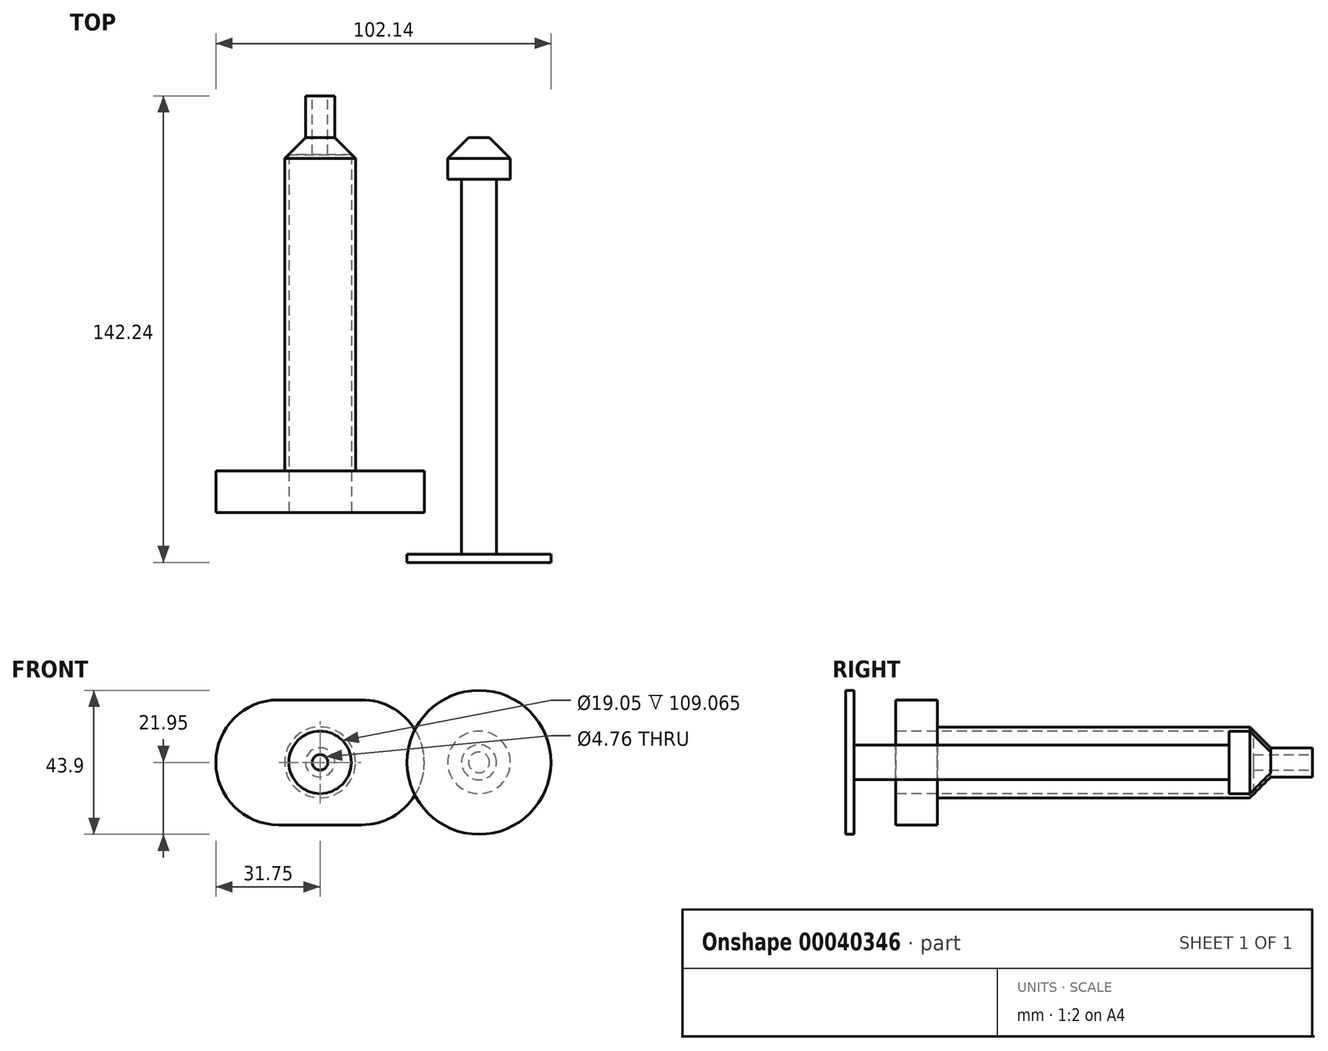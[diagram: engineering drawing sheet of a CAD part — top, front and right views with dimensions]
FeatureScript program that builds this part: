
annotation { "Feature Type Name" : "Feature", "Feature Type Description" : "" }
export const myFeature = defineFeature(function(context is Context, id is Id, definition is map)
    precondition{}
    {
        {
            var Q0;
            Q0=qCreatedBy(makeId("Front.planeOp"),FACE);
            var sketch = newSketch(context, id + "F0", { "sketchPlane" : qUnion([Q0])});
            skCircle(sketch, "E0", {"center": v(0, 0) * mm, "radius": 10.8 * mm});
            skCircle(sketch, "E1", {"center": v(48.44, 0) * mm, "radius": 9.53 * mm});
            skSolve(sketch);
        }
        {
            var Q0;
            Q0=makeQuery(id+"F0.imprint","IMPRINT",FACE,{"disambiguationData":[TD([[makeQuery(id+"F0.imprint","IMPRINT",EDGE,{"derivedFrom":sQuery(id+"F0.wireOp",EDGE,"E0")}),1.0]])]});
            extrude(context, id + "F1", {"entities" : qUnion([Q0]), "depth" : 101.6 * mm});
        }
        {
            var Q0;
            Q0=makeQuery(id+"F1.opExtrude","CAP_EDGE",EDGE,{"disambiguationData":[OSD([sQuery(id+"F0.wireOp",EDGE,"E0")])],"isStart":true});
            chamfer(context, id + "F2", {"entities" : qUnion([Q0]), "width" : 6.35 * mm, "tangentPropagation" : true});
        }
        {
            var Q0;
            Q0=makeQuery(id+"F1.opExtrude","CAP_FACE",FACE,{"disambiguationData":[OSD([sQuery(id+"F0.wireOp",EDGE,"E0")])],"isStart":true});
            extrude(context, id + "F3", {"entities" : qUnion([Q0]), "operationType" : NewBodyOperationType.ADD, "depth" : 12.7 * mm});
        }
        {
            var Q0;
            Q0=makeQuery(id+"F1.opExtrude","CAP_FACE",FACE,{"disambiguationData":[OSD([sQuery(id+"F0.wireOp",EDGE,"E0")])],"isStart":false});
            var sketch = newSketch(context, id + "F4", { "sketchPlane" : qUnion([Q0])});
            skLineSegment(sketch, "E2.rect.bottom", {"start": v(31.75, -19.05) * mm, "end": v(-31.75, -19.05) * mm});
            skLineSegment(sketch, "E2.rect.top", {"start": v(31.75, 19.05) * mm, "end": v(-31.75, 19.05) * mm});
            skLineSegment(sketch, "E2.rect.left", {"start": v(31.75, -19.05) * mm, "end": v(31.75, 19.05) * mm});
            skLineSegment(sketch, "E2.rect.right", {"start": v(-31.75, -19.05) * mm, "end": v(-31.75, 19.05) * mm});
            skPoint(sketch, "E2.rect.middle", {"position": v(0, 0) * mm});
            skSolve(sketch);
        }
        {
            var Q0;
            Q0 = qSketchRegion(id + "F4", true);
            extrude(context, id + "F5", {"entities" : qUnion([Q0]), "operationType" : NewBodyOperationType.ADD, "depth" : 12.7 * mm});
        }
        {
            var Q0;
            Q0=makeQuery(id+"F5.opExtrude","SWEPT_EDGE",EDGE,{"disambiguationData":[OSD([sQuery(id+"F4.wireOp",EDGE,"E2.rect.top"),sQuery(id+"F4.wireOp",EDGE,"E2.rect.right")])]});
            var Q1;
            Q1=makeQuery(id+"F5.opExtrude","SWEPT_EDGE",EDGE,{"disambiguationData":[OSD([sQuery(id+"F4.wireOp",EDGE,"E2.rect.top"),sQuery(id+"F4.wireOp",EDGE,"E2.rect.left")])]});
            var Q2;
            Q2=makeQuery(id+"F5.opExtrude","SWEPT_EDGE",EDGE,{"disambiguationData":[OSD([sQuery(id+"F4.wireOp",EDGE,"E2.rect.bottom"),sQuery(id+"F4.wireOp",EDGE,"E2.rect.left")])]});
            var Q3;
            Q3=makeQuery(id+"F5.opExtrude","SWEPT_EDGE",EDGE,{"disambiguationData":[OSD([sQuery(id+"F4.wireOp",EDGE,"E2.rect.bottom"),sQuery(id+"F4.wireOp",EDGE,"E2.rect.right")])]});
            fillet(context, id + "F6", {"entities" : qUnion([Q0, Q1, Q2, Q3]), "radius" : 19.05 * mm, "tangentPropagation" : true, "allowEdgeOverflow" : false});
        }
        {
            var Q0;
            Q0=makeQuery(id+"F5.opExtrude","CAP_FACE",FACE,{"disambiguationData":[OSD([sQuery(id+"F4.wireOp",EDGE,"E2.rect.bottom"),sQuery(id+"F4.wireOp",EDGE,"E2.rect.top"),sQuery(id+"F4.wireOp",EDGE,"E2.rect.left"),sQuery(id+"F4.wireOp",EDGE,"E2.rect.right")])],"isStart":false});
            var sketch = newSketch(context, id + "F7", { "sketchPlane" : qUnion([Q0])});
            skCircle(sketch, "E3", {"center": v(0, 0) * mm, "radius": 9.53 * mm});
            skSolve(sketch);
        }
        {
            var Q0;
            Q0=makeQuery(id+"F7.imprint","IMPRINT",FACE,{"disambiguationData":[TD([[makeQuery(id+"F7.imprint","IMPRINT",EDGE,{"derivedFrom":sQuery(id+"F7.wireOp",EDGE,"E3")}),1.0]])]});
            extrude(context, id + "F8", {"entities" : qUnion([Q0]), "operationType" : NewBodyOperationType.REMOVE, "oppositeDirection" : true, "depth" : 109.07 * mm});
        }
        {
            var Q0;
            Q0=makeQuery(id+"F3.opExtrude","CAP_FACE",FACE,{"disambiguationData":[OSD([sQuery(id+"F0.wireOp",EDGE,"E0")])],"isStart":false});
            var sketch = newSketch(context, id + "F9", { "sketchPlane" : qUnion([Q0])});
            skCircle(sketch, "E4", {"center": v(0, 0) * mm, "radius": 2.38 * mm});
            skSolve(sketch);
        }
        {
            var Q0;
            Q0 = qSketchRegion(id + "F9", true);
            extrude(context, id + "F10", {"entities" : qUnion([Q0]), "operationType" : NewBodyOperationType.REMOVE, "oppositeDirection" : true, "depth" : 87.48 * mm});
        }
        {
            var Q0;
            Q0=makeQuery(id+"F0.imprint","IMPRINT",FACE,{"disambiguationData":[TD([[makeQuery(id+"F0.imprint","IMPRINT",EDGE,{"derivedFrom":sQuery(id+"F0.wireOp",EDGE,"E0")}),1.0]])]});
            extrude(context, id + "F11", {"entities" : qUnion([Q0]), "depth" : 12.7 * mm});
        }
        {
            var Q0;
            Q0=makeQuery(id+"F0.imprint","IMPRINT",FACE,{"disambiguationData":[TD([[makeQuery(id+"F0.imprint","IMPRINT",EDGE,{"derivedFrom":sQuery(id+"F0.wireOp",EDGE,"E1")}),1.0]])]});
            extrude(context, id + "F12", {"entities" : qUnion([Q0]), "depth" : 12.7 * mm});
        }
        {
            var Q0;
            Q0=makeQuery(id+"F12.opExtrude","CAP_EDGE",EDGE,{"disambiguationData":[OSD([sQuery(id+"F0.wireOp",EDGE,"E1")])],"isStart":true});
            chamfer(context, id + "F13", {"entities" : qUnion([Q0]), "width" : 6.35 * mm, "tangentPropagation" : true});
        }
        {
            var Q0;
            Q0=makeQuery(id+"F12.opExtrude","CAP_FACE",FACE,{"disambiguationData":[OSD([sQuery(id+"F0.wireOp",EDGE,"E1")])],"isStart":false});
            var sketch = newSketch(context, id + "F14", { "sketchPlane" : qUnion([Q0])});
            skCircle(sketch, "E5", {"center": v(48.44, 0) * mm, "radius": 5.32 * mm});
            skSolve(sketch);
        }
        {
            var Q0;
            Q0 = qSketchRegion(id + "F14", true);
            extrude(context, id + "F15", {"entities" : qUnion([Q0]), "operationType" : NewBodyOperationType.ADD, "depth" : 114.3 * mm});
        }
        {
            var Q0;
            Q0=makeQuery(id+"F15.opExtrude","CAP_FACE",FACE,{"disambiguationData":[OSD([sQuery(id+"F14.wireOp",EDGE,"E5")])],"isStart":false});
            var sketch = newSketch(context, id + "F16", { "sketchPlane" : qUnion([Q0])});
            skCircle(sketch, "E6", {"center": v(48.44, 0) * mm, "radius": 21.95 * mm});
            skSolve(sketch);
        }
        {
            var Q0;
            Q0 = qSketchRegion(id + "F16", true);
            extrude(context, id + "F17", {"entities" : qUnion([Q0]), "operationType" : NewBodyOperationType.ADD, "depth" : 2.54 * mm});
        }
        {
            var Q0;
            Q0=makeQuery(id+"F11.opExtrude","SWEPT_BODY",BODY,{"disambiguationData":[OSD([sQuery(id+"F0.wireOp",EDGE,"E0")])]});
            deleteBodies(context, id + "F18", {"entities" : qUnion([Q0])});
        }
    });
